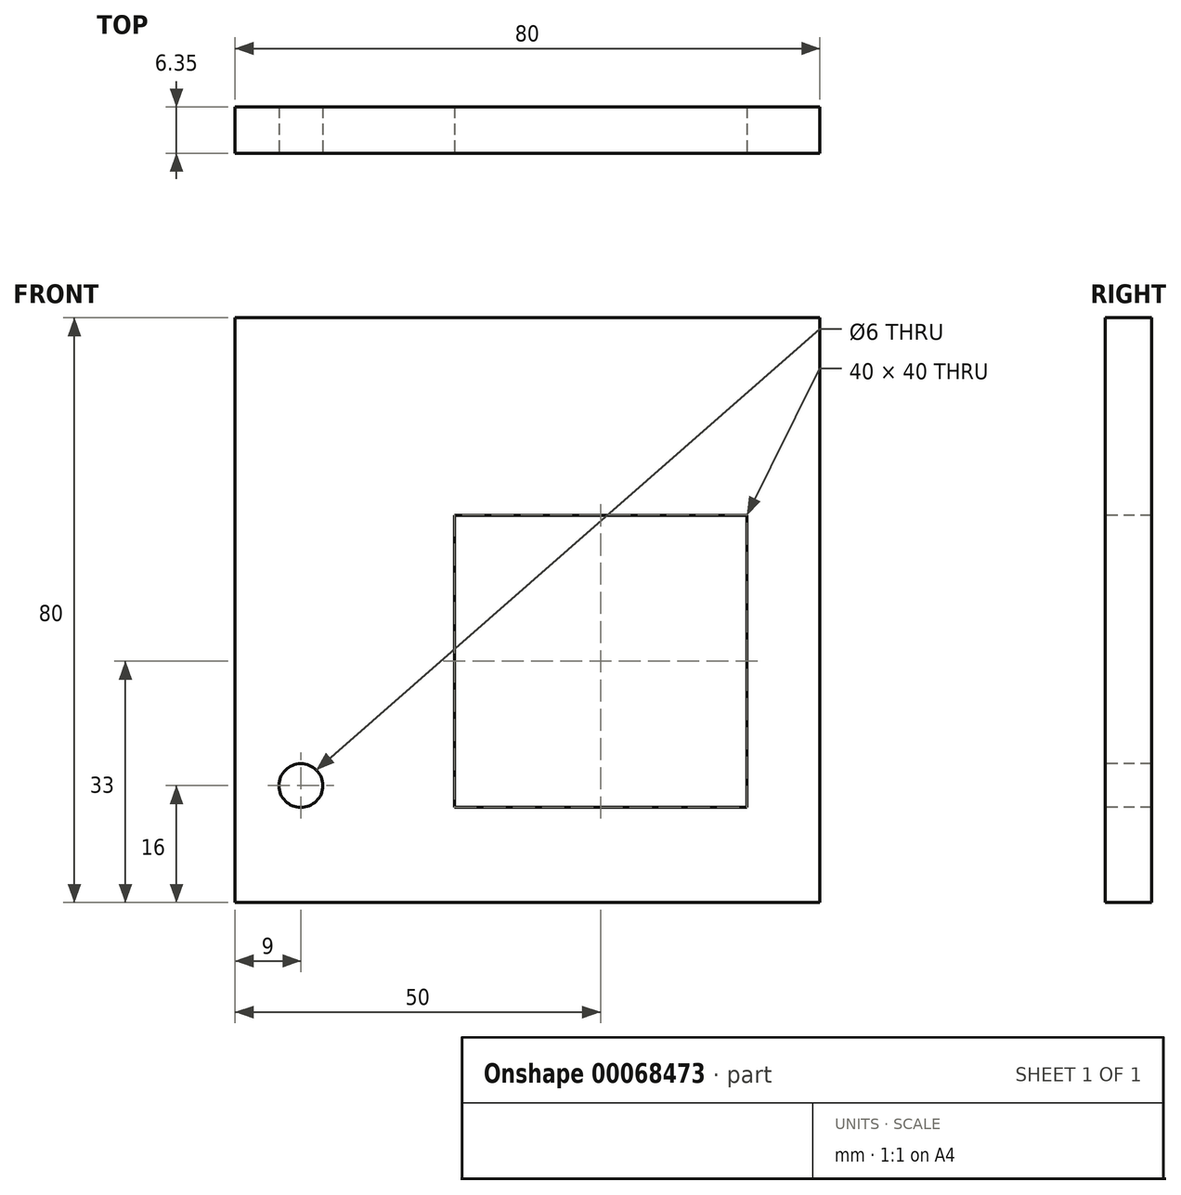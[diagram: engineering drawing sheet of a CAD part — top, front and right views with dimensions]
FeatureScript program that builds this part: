
annotation { "Feature Type Name" : "Feature", "Feature Type Description" : "" }
export const myFeature = defineFeature(function(context is Context, id is Id, definition is map)
    precondition{}
    {
        {
            var Q0;
            Q0=qCreatedBy(makeId("Front.planeOp"),FACE);
            var sketch = newSketch(context, id + "F0", { "sketchPlane" : qUnion([Q0])});
            skLineSegment(sketch, "E0.rect.bottom", {"start": v(40, -40) * mm, "end": v(-40, -40) * mm});
            skLineSegment(sketch, "E0.rect.top", {"start": v(40, 40) * mm, "end": v(-40, 40) * mm});
            skLineSegment(sketch, "E0.rect.left", {"start": v(40, -40) * mm, "end": v(40, 40) * mm});
            skLineSegment(sketch, "E0.rect.right", {"start": v(-40, -40) * mm, "end": v(-40, 40) * mm});
            skPoint(sketch, "E0.rect.middle", {"position": v(0, 0) * mm});
            skSolve(sketch);
        }
        {
            var Q0;
            Q0 = qSketchRegion(id + "F0", true);
            extrude(context, id + "F1", {"entities" : qUnion([Q0]), "depth" : 6.35 * mm});
        }
        {
            var Q0;
            Q0=makeQuery(id+"F1.opExtrude","CAP_FACE",FACE,{"disambiguationData":[OSD([sQuery(id+"F0.wireOp",EDGE,"E0.rect.bottom"),sQuery(id+"F0.wireOp",EDGE,"E0.rect.top"),sQuery(id+"F0.wireOp",EDGE,"E0.rect.left"),sQuery(id+"F0.wireOp",EDGE,"E0.rect.right")])],"isStart":false});
            var sketch = newSketch(context, id + "F2", { "sketchPlane" : qUnion([Q0])});
            skLineSegment(sketch, "E1.bottom", {"start": v(30, -27) * mm, "end": v(-10, -27) * mm});
            skLineSegment(sketch, "E1.top", {"start": v(30, 13) * mm, "end": v(-10, 13) * mm});
            skLineSegment(sketch, "E1.left", {"start": v(30, -27) * mm, "end": v(30, 13) * mm});
            skLineSegment(sketch, "E1.right", {"start": v(-10, -27) * mm, "end": v(-10, 13) * mm});
            skCircle(sketch, "E2", {"center": v(-31, -24) * mm, "radius": 3 * mm});
            skSolve(sketch);
        }
        {
            var Q0;
            Q0=makeQuery(id+"F2.imprint","IMPRINT",FACE,{"disambiguationData":[TD([[makeQuery(id+"F2.imprint","IMPRINT",EDGE,{"derivedFrom":sQuery(id+"F2.wireOp",EDGE,"E1.bottom")}),-1.0]])]});
            var Q1;
            Q1=makeQuery(id+"F2.imprint","IMPRINT",FACE,{"disambiguationData":[TD([[makeQuery(id+"F2.imprint","IMPRINT",EDGE,{"derivedFrom":sQuery(id+"F2.wireOp",EDGE,"E2")}),1.0]])]});
            extrude(context, id + "F3", {"entities" : qUnion([Q0, Q1]), "operationType" : NewBodyOperationType.REMOVE, "endBound" : BoundingType.THROUGH_ALL, "oppositeDirection" : true, "depth" : 25 * mm});
        }
    });
